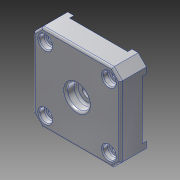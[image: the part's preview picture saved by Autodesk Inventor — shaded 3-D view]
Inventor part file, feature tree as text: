
AUTODESK INVENTOR PART (.ipt)
format: ipt  version: 2015 (Build 190159000, 159)  size: 226,304 bytes
history: native  units: mm
features: hole x4, extrude x3, fillet x3, sketch x3, pattern_linear x2
ambient origin geometry x8: Origin, YZ Plane, XZ Plane, XY Plane, X Axis, Y Axis, Z Axis, Center Point
bodies: Solid1 (feature_tree)
feature tree (15):
  extrude  "Extrusion1"  Depth=42.3mm
  extrude  "Extrusion2"  Depth=10.5mm
  extrude  "Extrusion3"  Depth=10.5mm TaperAngle=0.0deg
  hole  "Hole1"  [1 undecoded]
  hole  "Hole2"  [1 undecoded]
  pattern_linear  "Rectangular Pattern1"  Spacing1=21.15mm  [1 undecoded]
  hole  "Hole3"  [1 undecoded]
  hole  "Hole4"  [1 undecoded]
  pattern_linear  "Rectangular Pattern2"  Count1=2 Spacing1=31.0mm
  fillet  "Fillet1"  Radius=21.15mm
  fillet  "Fillet2"  Radius=5.65mm
  fillet  "Fillet3"  Radius=20.0mm
  sketch  "Sketch1"  dims[d0=42.3mm d1=42.3mm]
  sketch  "Sketch2"  dims[d2=10.5mm d3=0.0mm d4=5.657mm]
  sketch  "Sketch3"  dims[d5=135.0deg d6=10.5mm d7=0.0mm d8=2.121mm d9=2.121mm d10=0.0mm d11=21.15mm d12=21.15mm d13=5.0mm d14=6.0mm d15=4.0mm d16=2.0mm d17=90.0deg d18=8.0mm d19=20.594885mm d20=5.65mm d21=5.65mm d22=3.0mm d23=6.0mm d24=4.0mm d25=2.0mm d26=90.0deg d27=8.0mm d28=20.594885mm d29=20.0mm d31=31.0mm d32=20.0mm d34=31.0mm d35=21.15mm d36=21.15mm d37=11.0mm d38=6.0mm d39=4.0mm d40=2.0mm d41=90.0deg d42=5.0mm d43=0.0mm d44=5.65mm d45=5.65mm d46=6.2mm d47=6.0mm d48=4.0mm d49=2.0mm d50=90.0deg d51=3.0mm d52=0.0mm d53=20.0mm d55=31.0mm d56=20.0mm d58=31.0mm d59=1.0mm d60=0.5mm d61=1.0mm]
note: 5 required parameter values undecoded (feature->parameter linkage not recoverable at this tier; creation-order binding heuristic only, values carry confidence <= 0.55)
